# Revit family: Elevators-and-Lifts_Twin-Jack-Holeless_Delaware_Elevator
name_source: partatom
category: Specialty Equipment
units: mm (PartAtom-declared; Revit-internal decimal feet)

## family parameters
Always vertical = Yes
Cut with Voids When Loaded = No
Enable Cutting in Views = No
Maintain Annotation Orientation = No
Part Type = Normal
Room Calculation Point = No
Round Connector Dimension = Use Diameter
Shared = No
Work Plane-Based = No

## types (18) — shared parameters
Cabin Height = 8' - 2"
Cabin offset from Level-01 = 0' - 0"
Default Elevation = 0' - 0"
Keynote = 14 40 00
Manufacturer = Delaware Elevator Manufacturing
Opening Height = 7' - 0"
Product Page URL = https://www.arcat.com
R1 = 103' - 8 13/16"
Sump Pit Depth = 2' - 0"
Sump Pit Height = 1' - 2"
URL = https://delawareelevator.com
X1 = 26' - 3"

## per-type parameters (varying)
| type | Cabin Depth | Cabin F&R_Depth | Cabin F&R_Width | Cabin Width | Front & Rear Door | Front Door | Opening Width | Pit Depth | Pit Width | Sump Pit Width | Wall Thickness |
| DEI-2100-DH | 4' - 3" | 3' - 6" | 5' - 8" | 5' - 8" | No | Yes | 3' - 6" | 5' - 10" | 7' - 4" | 1' - 6" | 0' - 8" |
| DEI-2100-DH-FR | 5' - 1" | 4' - 4" | 5' - 8" | 5' - 8" | Yes | No | 3' - 6" | 6' - 8" | 7' - 4" | 2' - 0" | 0' - 8" |
| DEI-2500-DH | 4' - 3" | 3' - 6" | 6' - 8" | 6' - 8" | No | Yes | 3' - 6" | 5' - 10" | 8' - 4" | 2' - 0" | 0' - 11" |
| DEI-2500-DH-FR | 5' - 1" | 4' - 4" | 6' - 8" | 6' - 8" | Yes | No | 3' - 3 1/2" | 6' - 8" | 8' - 4" | 1' - 3 1/2" | 0' - 8" |
| DEI-3000-DH | 4' - 8" | 3' - 11" | 6' - 8" | 6' - 8" | No | Yes | 3' - 3 1/2" | 6' - 3" | 8' - 4" | 1' - 3 1/2" | 0' - 8" |
| DEI-3000-DH-FR | 5' - 4" | 4' - 7" | 6' - 8" | 6' - 8" | Yes | No | 3' - 3 1/2" | 6' - 11" | 8' - 4" | 1' - 3 1/2" | 0' - 8" |
| DEI-3500-DH | 5' - 5" | 4' - 8" | 6' - 8" | 6' - 8" | No | Yes | 3' - 3 1/2" | 7' - 0" | 8' - 4" | 1' - 3 1/2" | 0' - 8" |
| DEI-3500-DH-FR | 6' - 2" | 5' - 5" | 6' - 8" | 6' - 8" | Yes | No | 3' - 3 1/2" | 7' - 9" | 8' - 4" | 1' - 3 1/2" | 0' - 8" |
| DEI-3500H-DH | 7' - 8" | 6' - 11" | 5' - 0" | 5' - 0" | No | Yes | 3' - 6" | 9' - 3" | 6' - 8" | 1' - 3 1/2" | 0' - 8" |
| DEI-3500H-DH-FR | 8' - 8" | 7' - 11" | 5' - 0" | 5' - 0" | Yes | No | 3' - 6" | 10' - 3" | 6' - 8" | 1' - 3 1/2" | 0' - 8" |
| DEI-4000-DH | 5' - 5" | 4' - 8" | 7' - 8" | 7' - 8" | No | Yes | 3' - 6" | 7' - 0" | 9' - 4" | 1' - 3 1/2" | 0' - 8" |
| DEI-4000-DH-FR | 6' - 2" | 5' - 5" | 7' - 8" | 7' - 8" | Yes | No | 4' - 0" | 7' - 9" | 9' - 4" | 1' - 3 1/2" | 0' - 8" |
| DEI-4000H-DH | 7' - 7 1/2" | 6' - 10 1/2" | 5' - 8" | 5' - 8" | No | Yes | 4' - 0" | 9' - 2 1/2" | 7' - 4" | 1' - 3 1/2" | 0' - 8" |
| DEI-4000H-DH-FR | 8' - 9" | 8' - 0" | 5' - 8" | 5' - 8" | Yes | No | 4' - 0" | 10' - 4" | 7' - 4" | 1' - 3 1/2" | 0' - 8" |
| DEI-4500-DH | 8' - 0" | 7' - 3" | 5' - 8" | 5' - 8" | No | Yes | 4' - 0" | 9' - 7" | 7' - 4" | 1' - 3 1/2" | 0' - 8" |
| DEI-4500H-DH-FR | 9' - 2" | 8' - 5" | 5' - 8" | 5' - 8" | Yes | No | 4' - 0" | 10' - 9" | 7' - 4" | 1' - 3 1/2" | 0' - 8" |
| DEI-5000H-DH | 9' - 0" | 8' - 3" | 5' - 10" | 5' - 10" | No | Yes | 4' - 0" | 10' - 7" | 7' - 6" | 1' - 3 1/2" | 0' - 8" |
| DEI-5000H-DH-FR | 10' - 0" | 9' - 3" | 5' - 10" | 5' - 10" | Yes | No | 4' - 0" | 11' - 7" | 7' - 6" | 1' - 3 1/2" | 0' - 8" |

## geometry (parser evidence)
native form markers: Sweep x29
no freeform markers — native parametric forms only
